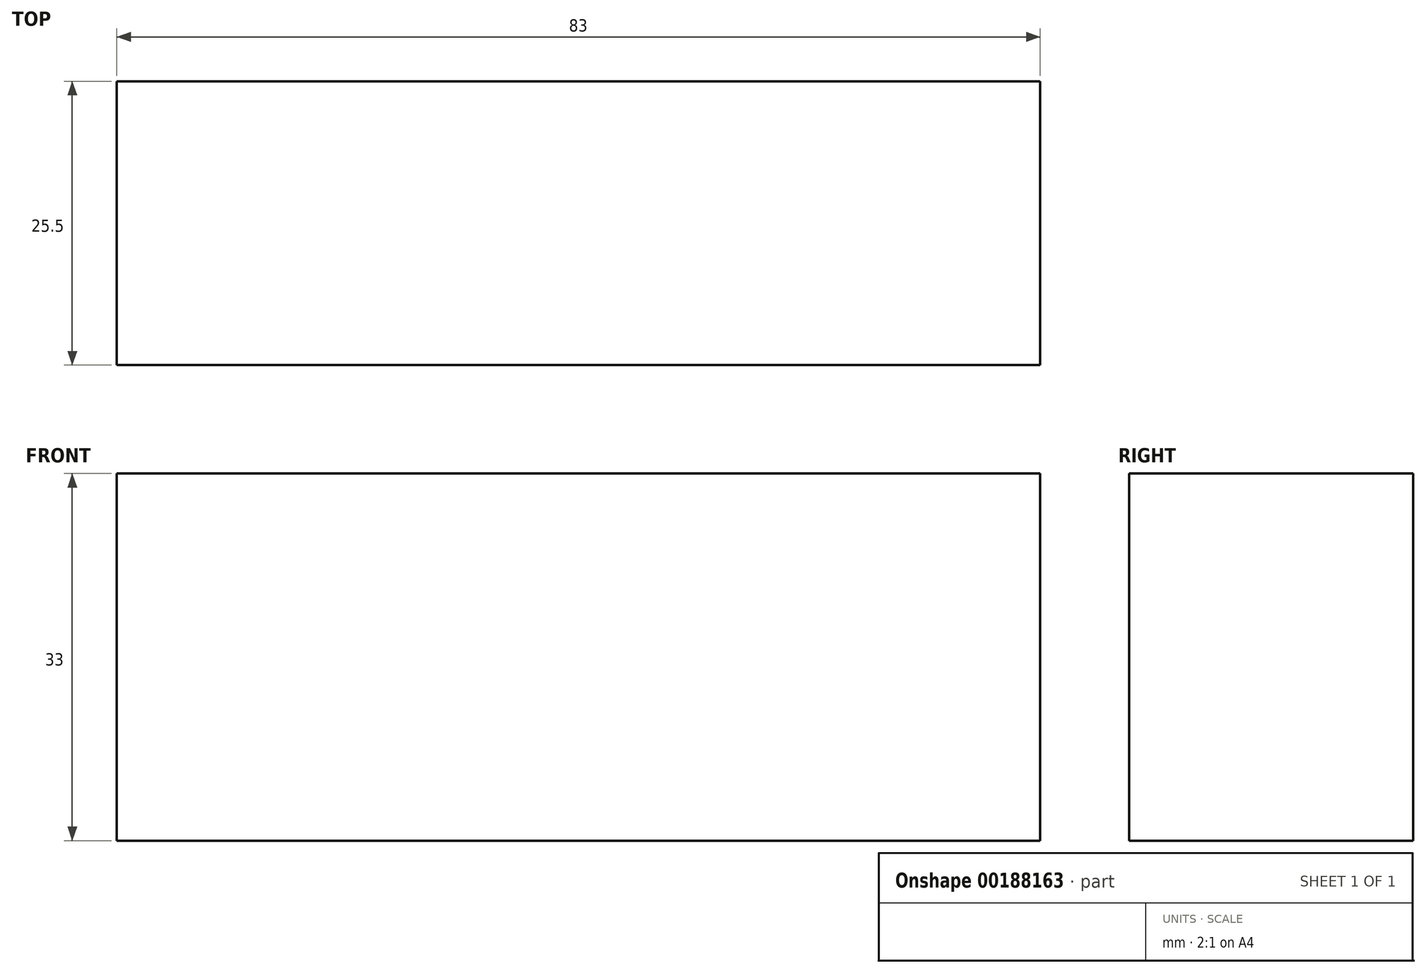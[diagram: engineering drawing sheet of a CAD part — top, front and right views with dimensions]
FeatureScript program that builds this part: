
annotation { "Feature Type Name" : "Feature", "Feature Type Description" : "" }
export const myFeature = defineFeature(function(context is Context, id is Id, definition is map)
    precondition{}
    {
        {
            var Q0;
            Q0=qCreatedBy(makeId("Front.planeOp"),FACE);
            var sketch = newSketch(context, id + "F0", { "sketchPlane" : qUnion([Q0])});
            skLineSegment(sketch, "E0.bottom", {"start": v(-40.36, 9.34) * mm, "end": v(42.64, 9.34) * mm});
            skLineSegment(sketch, "E0.top", {"start": v(-40.36, -23.66) * mm, "end": v(42.64, -23.66) * mm});
            skLineSegment(sketch, "E0.left", {"start": v(-40.36, 9.34) * mm, "end": v(-40.36, -23.66) * mm});
            skLineSegment(sketch, "E0.right", {"start": v(42.64, 9.34) * mm, "end": v(42.64, -23.66) * mm});
            skSolve(sketch);
        }
        {
            var Q0;
            Q0=qSketchRegion(id+"F0",true);
            extrude(context, id + "F1", {"entities" : qUnion([Q0]), "depth" : 25.5 * mm});
        }
    });
